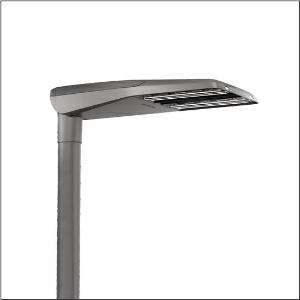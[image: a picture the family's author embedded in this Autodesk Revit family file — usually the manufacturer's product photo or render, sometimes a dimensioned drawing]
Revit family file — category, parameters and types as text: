
# Revit family: streetlight_sl_11_iq_midi___st1_2a_5xc3a11g08me_6871
name_source: partatom
category: Lighting Fixtures
units: mm (PartAtom-declared; Revit-internal decimal feet)

## family parameters
Cut with Voids When Loaded = No
Host = Face
Light Source = No
Part Type = Normal
Room Calculation Point = No
Round Connector Dimension = Use Diameter
Shared = No

## types (1)
- --- (1 x LED, 11170 lm, 124.5 W, 1800K)
    Apparent Load = 125 VA
    CIE Flux Codes = 32 70 96 100 100
    Color Rendering = 70
    Color Temperature = 1800K
    Default Elevation = 1800 mm  [stored 5.90551 ft]
    Description = Streetlight SL 11 iQ midi, mast luminaire, primary light control with 3 zone facetted reflector, of plastic, silver coated, highly specular, primary optical cover: cover, of PMMA, transparent, light distribution: ST1.2a, light emission: direct distribution, primary light characteristic: asymmetric, installation type: post-top, side-entry, LED, High Power LED, rated luminous flux: 11.170lm, luminous efficacy: 90lm/W, light colour: 718, colour temperature: 1800K, control: Street-Remote, Auto-Match, Temp-Guard, Lumen-Switch, Night-Set, Smart-Wire, Light-Fading, Desk-Remote (wireless, voltage-free reading and setting of iQ features in the workshop via application-optimized NFC function/RFID function), optimised constant luminous flux control (CLO 2.0), presetting dimming linear, with cable H07RN-F 5x 1.5mm², mains connection: 230..240V, AC, 50/60Hz, connection cable pre-assembled, cable length: 12,5m, start of lifetime: 125W, end of service life: 132W, reduction: 55W, luminaire housing, of diecast aluminium, powder-coated, Siteco® metallic grey (DB 702S), please order mast flange separately, inclination adjustable without tools: 0°, 5°, 10°, 15° (post-top) | 0°, -5°, -10°, -15° (side-entry), sealing non-destructively replaceable, multi-level sealing system, length: 780mm, width: 376mm, height: 118mm, mast flange for spigot size: 42mm (side-entry): 5XC10008XM4, 60/48mm (side-entry/post-top): 5XC10108XM2, 76/60mm (side-entry/post-top): 5XC10108XM1, equipment: Power, protection rating (complete): IP66, insulation class (complete): insulation class II (safety insulation), certification: CE, ENEC, VDE, impact resistance: IK09, permissible operating ambient temperature for outdoor applications: -25..+50°C, standard-compliant lighting for roads and squares, Environmental Product Declaration (EPD) tested and certified by an independent institute, packaging unit: 1 piece

Light Distribution: ST1.2a
    Height = 118 mm
    Lamp = 1 x LED
    Lamp Light Flux = 11170 lm
    Lamp Power = 124.5 W
    Lamp count = 1
    Length = 780 mm
    Luminous efficacy = 90 lm/W
    Manufacturer = Siteco
    ModVariant = No
    Model = 5XC3A11G08ME
    Number of Poles = 1
    OnlyDefault = Yes
    Power Factor = 1
    Product Name = Streetlight SL 11 iQ midi | ST1.2a
    Product group = mast luminaire | pylon top
    ProductGroupID = 6100
    Protection Class = Protection class II
    Protection Degree = IP 66
    RLX_Detail_Level = 1
    RLX_Emergency_Light_Flux = 0 lm
    RLX_Emergency_Type = 0
    RLX_Emergency_Type_DB = No
    RlxData = <blob elided: 70801 chars, md5=0527415c>
    Socket = socket
    Standby Power = 0 W
    System Light Flux = 11170 lm
    System Power = 125 W
    Type Comments = factory setting: luminous flux: 100 % | dim-lin: 254 | 554 mA
    Type Image = l_1005960.jpg
    URL = http://relux.com
    VarID = @adj_029367
    Voltage = 0 V
    Weight = 0.00 kg
    Width = 376 mm

note: [stored X ft] marks values corroborated as IEEE doubles in the binary element streams (Revit-internal decimal feet)

## geometry (parser evidence)
native form markers: Blend x4, Sweep x10
no freeform markers — native parametric forms only
